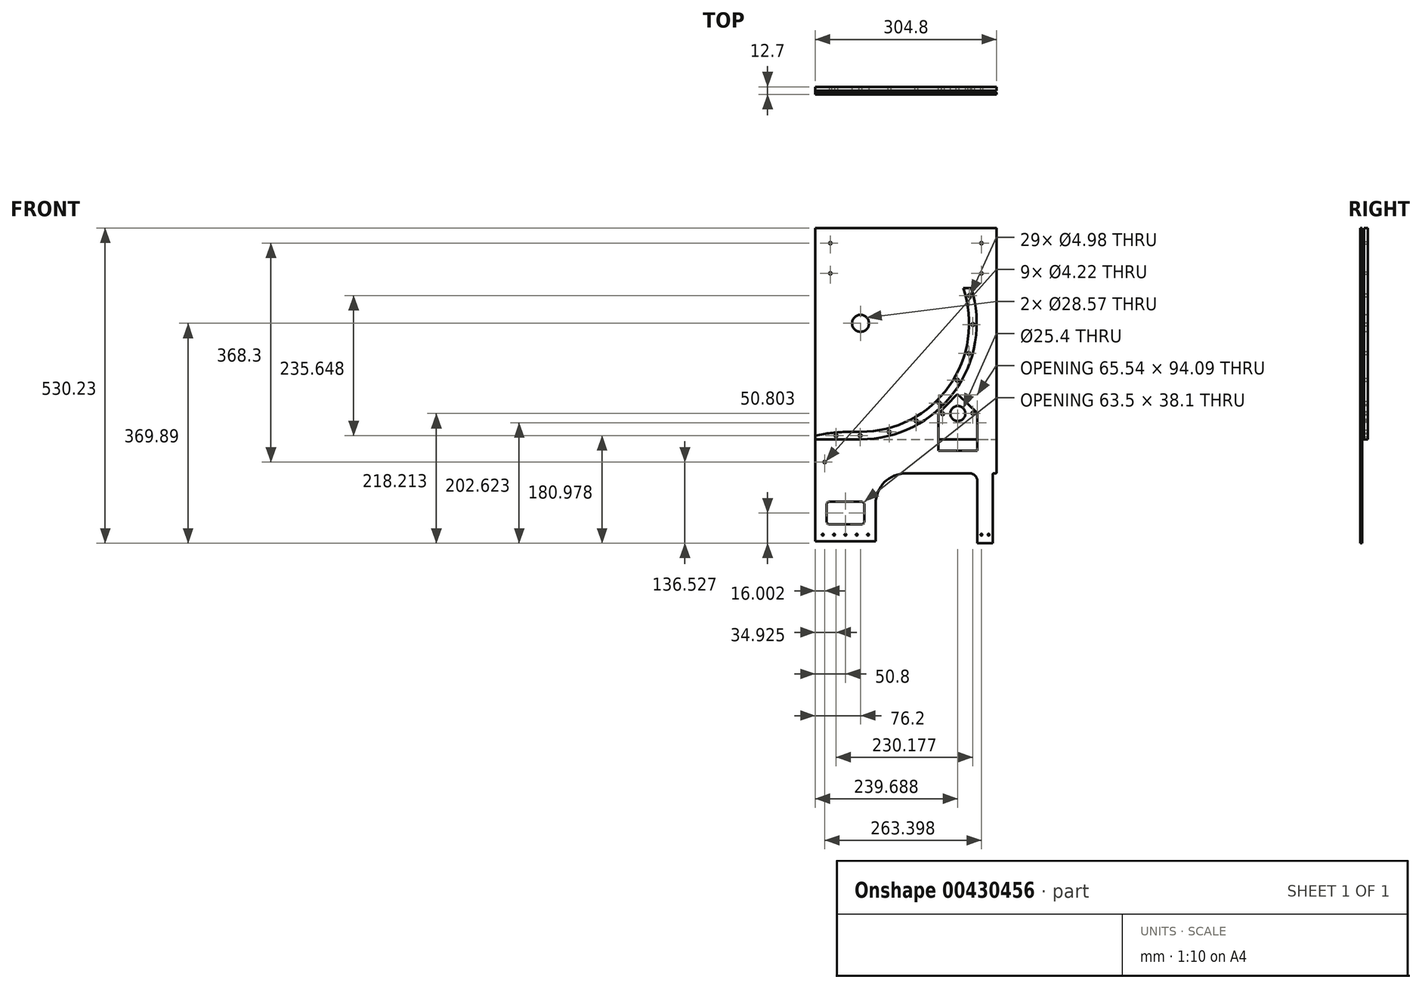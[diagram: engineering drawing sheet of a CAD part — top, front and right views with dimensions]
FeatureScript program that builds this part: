
annotation { "Feature Type Name" : "Feature", "Feature Type Description" : "" }
export const myFeature = defineFeature(function(context is Context, id is Id, definition is map)
    precondition{}
    {
        {
            var Q0;
            Q0=qCreatedBy(makeId("Front.planeOp"),FACE);
            var sketch = newSketch(context, id + "F0", { "sketchPlane" : qUnion([Q0])});
            skCircle(sketch, "E0", {"center": v(0, 0) * mm, "radius": 61.91 * mm, "construction": true});
            skArc(sketch, "E1", {"start": v(0, -182.56) * mm, "mid": v(148.63, -106.01) * mm, "end": v(172.62, 59.44) * mm});
            skLineSegment(sketch, "E2", {"start": v(228.6, -195.26) * mm, "end": v(228.6, 59.44) * mm, "construction": true});
            skLineSegment(sketch, "E3", {"start": v(228.6, 59.44) * mm, "end": v(172.62, 59.44) * mm});
            skLineSegment(sketch, "E4", {"start": v(0, 0) * mm, "end": v(182.56, 0) * mm, "construction": true});
            skLineSegment(sketch, "E5", {"start": v(0, 0) * mm, "end": v(172.62, 59.44) * mm, "construction": true});
            skLineSegment(sketch, "E6", {"start": v(209.55, -195.26) * mm, "end": v(209.55, 59.44) * mm, "construction": true});
            skPoint(sketch, "E7.middle", {"position": v(163.49, -151.68) * mm});
            skLineSegment(sketch, "E8.top", {"start": v(228.6, -195.26) * mm, "end": v(-76.2, -195.26) * mm});
            skLineSegment(sketch, "E8.right", {"start": v(-76.2, -188.91) * mm, "end": v(-76.2, -195.26) * mm});
            skLineSegment(sketch, "E9", {"start": v(0, -182.56) * mm, "end": v(-41.27, -182.56) * mm});
            skCircle(sketch, "E10", {"center": v(163.49, -151.68) * mm, "radius": 25.4 * mm, "construction": true});
            skLineSegment(sketch, "E11", {"start": v(130.72, -152.33) * mm, "end": v(162.84, -118.9) * mm, "construction": true});
            skLineSegment(sketch, "E12", {"start": v(162.84, -118.9) * mm, "end": v(196.26, -151.03) * mm, "construction": true});
            skLineSegment(sketch, "E13", {"start": v(196.26, -151.03) * mm, "end": v(164.14, -184.45) * mm, "construction": true});
            skLineSegment(sketch, "E14", {"start": v(164.14, -184.45) * mm, "end": v(130.72, -152.33) * mm, "construction": true});
            skLineSegment(sketch, "E15", {"start": v(162.84, -118.9) * mm, "end": v(164.14, -184.45) * mm, "construction": true});
            skCircle(sketch, "E16", {"center": v(183.04, 46.74) * mm, "radius": 2.49 * mm});
            skCircle(sketch, "E17.1.0", {"center": v(188.9, -2) * mm, "radius": 2.49 * mm});
            skCircle(sketch, "E17.2.0", {"center": v(182.01, -50.6) * mm, "radius": 2.49 * mm});
            skCircle(sketch, "E17.3.0", {"center": v(162.84, -95.77) * mm, "radius": 2.49 * mm});
            skCircle(sketch, "E17.4.0", {"center": v(132.67, -134.49) * mm, "radius": 2.49 * mm});
            skCircle(sketch, "E17.5.0", {"center": v(93.54, -164.13) * mm, "radius": 2.49 * mm});
            skCircle(sketch, "E17.6.0", {"center": v(48.1, -182.69) * mm, "radius": 2.49 * mm});
            skCircle(sketch, "E17.7.0", {"center": v(-0.58, -188.91) * mm, "radius": 2.49 * mm});
            skLineSegment(sketch, "E17.anchor1", {"start": v(0, 0) * mm, "end": v(183.04, 46.74) * mm, "construction": true});
            skLineSegment(sketch, "E17.anchor2", {"start": v(0, 0) * mm, "end": v(-0.58, -188.91) * mm, "construction": true});
            skLineSegment(sketch, "E18", {"start": v(130.72, -152.33) * mm, "end": v(130.72, -195.26) * mm, "construction": true});
            skLineSegment(sketch, "E19", {"start": v(196.26, -151.03) * mm, "end": v(196.26, -195.26) * mm, "construction": true});
            skCircle(sketch, "E20", {"center": v(-41.27, -188.91) * mm, "radius": 2.49 * mm});
            skLineSegment(sketch, "E21", {"start": v(-76.2, -188.91) * mm, "end": v(-41.27, -182.56) * mm});
            skArc(sketch, "E22.trimOffspring", {"start": v(0, -195.26) * mm, "mid": v(157.7, -115.16) * mm, "end": v(186, 59.44) * mm});
            skPoint(sketch, "E23.orphan", {"position": v(-76.2, -182.56) * mm});
            skSolve(sketch);
        }
        {
            var Q0;
            {var subQ1=sQuery(id+"F0.wireOp",EDGE,"E8.top");var subQ5=sQuery(id+"F0.wireOp",EDGE,"E8.right");var subQ6=makeQuery(id+"F0.imprint","INTERSECT",VERTEX,{"derivedFrom":[subQ1,subQ5]});Q0=makeQuery(id+"F0.imprint","IMPRINT",FACE,{"disambiguationData":[TD([[makeQuery(id+"F0.imprint","IMPRINT",EDGE,{"disambiguationData":[TD([[subQ6,1.0]])],"derivedFrom":subQ1}),-1.0]])]});}
            var Q1;
            {var subQ0=sQuery(id+"F0.wireOp",EDGE,"E1");Q1=makeQuery(id+"F0.imprint","IMPRINT",FACE,{"disambiguationData":[TD([[makeQuery(id+"F0.imprint","IMPRINT",EDGE,{"derivedFrom":subQ0}),-1.0]])]});}
            extrude(context, id + "F1", {"entities" : qUnion([Q0, Q1]), "depth" : 6.35 * mm, "offsetDistance" : 25.4 * mm});
        }
        {
            var Q0;
            {var subQ0=sQuery(id+"F0.wireOp",EDGE,"E1");Q0=makeQuery(id+"F0.imprint","IMPRINT",FACE,{"disambiguationData":[TD([[makeQuery(id+"F0.imprint","IMPRINT",EDGE,{"derivedFrom":subQ0}),-1.0]])]});}
            var sketch = newSketch(context, id + "F2", { "sketchPlane" : qUnion([Q0])});
            skCircle(sketch, "E24", {"center": v(0, 0) * mm, "radius": 14.29 * mm});
            skLineSegment(sketch, "E25.bottom", {"start": v(-76.2, -252.41) * mm, "end": v(228.6, -252.41) * mm});
            skLineSegment(sketch, "E25.top", {"start": v(-76.2, 160.34) * mm, "end": v(228.6, 160.34) * mm});
            skLineSegment(sketch, "E25.left", {"start": v(-76.2, -252.41) * mm, "end": v(-76.2, 160.34) * mm});
            skLineSegment(sketch, "E25.right", {"start": v(228.6, -252.41) * mm, "end": v(228.6, 160.34) * mm});
            skPoint(sketch, "E26.0", {"position": v(183.04, 46.74) * mm});
            skCircle(sketch, "E27.0", {"center": v(188.9, -2) * mm, "radius": 2.49 * mm});
            skCircle(sketch, "E27.1", {"center": v(183.04, 46.74) * mm, "radius": 2.49 * mm});
            skCircle(sketch, "E27.2", {"center": v(182.01, -50.6) * mm, "radius": 2.49 * mm});
            skCircle(sketch, "E27.3", {"center": v(162.84, -95.77) * mm, "radius": 2.49 * mm});
            skCircle(sketch, "E27.4", {"center": v(132.67, -134.49) * mm, "radius": 2.49 * mm});
            skCircle(sketch, "E27.5", {"center": v(93.54, -164.13) * mm, "radius": 2.49 * mm});
            skCircle(sketch, "E27.6", {"center": v(48.1, -182.69) * mm, "radius": 2.49 * mm});
            skCircle(sketch, "E27.7", {"center": v(-0.58, -188.91) * mm, "radius": 2.49 * mm});
            skCircle(sketch, "E27.8", {"center": v(-41.27, -188.91) * mm, "radius": 2.49 * mm});
            skCircle(sketch, "E28.0", {"center": v(163.49, -151.68) * mm, "radius": 25.4 * mm, "construction": true});
            skPoint(sketch, "E29.0", {"position": v(130.72, -152.33) * mm});
            skPoint(sketch, "E29.1", {"position": v(196.26, -151.03) * mm});
            skLineSegment(sketch, "E30", {"start": v(130.72, -152.33) * mm, "end": v(196.26, -151.03) * mm, "construction": true});
            skCircle(sketch, "E31", {"center": v(138.1, -152.18) * mm, "radius": 2.49 * mm});
            skCircle(sketch, "E32", {"center": v(188.88, -151.17) * mm, "radius": 2.49 * mm});
            skCircle(sketch, "E33", {"center": v(346.2, -207.96) * mm, "radius": 2.1 * mm});
            skLineSegment(sketch, "E34.bottom", {"start": v(-76.2, -195.26) * mm, "end": v(381, -195.26) * mm});
            skLineSegment(sketch, "E34.top", {"start": v(-76.2, -252.41) * mm, "end": v(381, -252.41) * mm});
            skLineSegment(sketch, "E34.left", {"start": v(-76.2, -195.26) * mm, "end": v(-76.2, -252.41) * mm});
            skLineSegment(sketch, "E34.right", {"start": v(381, -195.26) * mm, "end": v(381, -252.41) * mm});
            skCircle(sketch, "E35.0.1.0", {"center": v(346.2, -233.36) * mm, "radius": 2.1 * mm});
            skCircle(sketch, "E35.1.0.0", {"center": v(320.8, -207.96) * mm, "radius": 2.1 * mm});
            skCircle(sketch, "E35.1.1.0", {"center": v(320.8, -233.36) * mm, "radius": 2.1 * mm});
            skCircle(sketch, "E35.2.0.0", {"center": v(295.4, -207.96) * mm, "radius": 2.1 * mm});
            skCircle(sketch, "E35.2.1.0", {"center": v(295.4, -233.36) * mm, "radius": 2.1 * mm});
            skCircle(sketch, "E35.3.0.0", {"center": v(270, -207.96) * mm, "radius": 2.1 * mm});
            skCircle(sketch, "E35.3.1.0", {"center": v(270, -233.36) * mm, "radius": 2.1 * mm});
            skCircle(sketch, "E35.4.0.0", {"center": v(244.6, -207.96) * mm, "radius": 2.1 * mm});
            skCircle(sketch, "E35.4.1.0", {"center": v(244.6, -233.36) * mm, "radius": 2.1 * mm});
            skCircle(sketch, "E35.5.0.0", {"center": v(219.2, -207.96) * mm, "radius": 2.1 * mm});
            skCircle(sketch, "E35.5.1.0", {"center": v(219.2, -233.36) * mm, "radius": 2.1 * mm});
            skCircle(sketch, "E35.6.0.0", {"center": v(193.8, -207.96) * mm, "radius": 2.1 * mm});
            skCircle(sketch, "E35.6.1.0", {"center": v(193.8, -233.36) * mm, "radius": 2.1 * mm});
            skCircle(sketch, "E35.7.0.0", {"center": v(168.4, -207.96) * mm, "radius": 2.1 * mm});
            skCircle(sketch, "E35.7.1.0", {"center": v(168.4, -233.36) * mm, "radius": 2.1 * mm});
            skCircle(sketch, "E35.8.0.0", {"center": v(143, -207.96) * mm, "radius": 2.1 * mm});
            skCircle(sketch, "E35.8.1.0", {"center": v(143, -233.36) * mm, "radius": 2.1 * mm});
            skCircle(sketch, "E35.9.0.0", {"center": v(117.6, -207.96) * mm, "radius": 2.1 * mm});
            skCircle(sketch, "E35.9.1.0", {"center": v(117.6, -233.36) * mm, "radius": 2.1 * mm});
            skCircle(sketch, "E35.10.0.0", {"center": v(92.2, -207.96) * mm, "radius": 2.1 * mm});
            skCircle(sketch, "E35.10.1.0", {"center": v(92.2, -233.36) * mm, "radius": 2.1 * mm});
            skCircle(sketch, "E35.11.0.0", {"center": v(66.8, -207.96) * mm, "radius": 2.1 * mm});
            skCircle(sketch, "E35.11.1.0", {"center": v(66.8, -233.36) * mm, "radius": 2.1 * mm});
            skCircle(sketch, "E35.12.0.0", {"center": v(41.4, -207.96) * mm, "radius": 2.1 * mm});
            skCircle(sketch, "E35.12.1.0", {"center": v(41.4, -233.36) * mm, "radius": 2.1 * mm});
            skCircle(sketch, "E35.13.0.0", {"center": v(16, -207.96) * mm, "radius": 2.1 * mm});
            skCircle(sketch, "E35.13.1.0", {"center": v(16, -233.36) * mm, "radius": 2.1 * mm});
            skCircle(sketch, "E35.14.0.0", {"center": v(-9.4, -207.96) * mm, "radius": 2.1 * mm});
            skCircle(sketch, "E35.14.1.0", {"center": v(-9.4, -233.36) * mm, "radius": 2.1 * mm});
            skCircle(sketch, "E35.15.0.0", {"center": v(-34.8, -207.96) * mm, "radius": 2.1 * mm});
            skCircle(sketch, "E35.15.1.0", {"center": v(-34.8, -233.36) * mm, "radius": 2.1 * mm});
            skCircle(sketch, "E35.16.0.0", {"center": v(-60.2, -207.96) * mm, "radius": 2.1 * mm});
            skCircle(sketch, "E35.16.1.0", {"center": v(-60.2, -233.36) * mm, "radius": 2.1 * mm});
            skLineSegment(sketch, "E35.direction1", {"start": v(346.2, -207.96) * mm, "end": v(320.8, -207.96) * mm, "construction": true});
            skLineSegment(sketch, "E35.direction2", {"start": v(346.2, -207.96) * mm, "end": v(346.2, -233.36) * mm, "construction": true});
            skCircle(sketch, "E36", {"center": v(163.49, -151.68) * mm, "radius": 12.7 * mm});
            skLineSegment(sketch, "E37", {"start": v(-50.8, 160.34) * mm, "end": v(-50.8, -195.26) * mm, "construction": true});
            skCircle(sketch, "E38", {"center": v(-50.8, 84.14) * mm, "radius": 2.1 * mm});
            skCircle(sketch, "E39.0.1.0", {"center": v(-50.8, 134.94) * mm, "radius": 2.1 * mm});
            skLineSegment(sketch, "E39.direction1", {"start": v(-50.8, 84.14) * mm, "end": v(-50.8, 84.14) * mm});
            skLineSegment(sketch, "E39.direction2", {"start": v(-50.8, 84.14) * mm, "end": v(-50.8, 134.94) * mm, "construction": true});
            skLineSegment(sketch, "E40", {"start": v(76.2, 160.34) * mm, "end": v(76.2, -195.26) * mm, "construction": true});
            skCircle(sketch, "E41.MirrorC", {"center": v(203.2, 84.14) * mm, "radius": 2.1 * mm});
            skCircle(sketch, "E42.MirrorC", {"center": v(203.2, 134.94) * mm, "radius": 2.1 * mm});
            skLineSegment(sketch, "E43.MirrorCS", {"start": v(203.2, 84.14) * mm, "end": v(203.2, 134.94) * mm, "construction": true});
            skLineSegment(sketch, "E44.0", {"start": v(0, -182.56) * mm, "end": v(-41.27, -182.56) * mm});
            skSolve(sketch);
        }
        {
            var Q0;
            {var subQ3=sQuery(id+"F2.wireOp",EDGE,"E34.left");Q0=makeQuery(id+"F2.imprint","IMPRINT",FACE,{"disambiguationData":[TD([[makeQuery(id+"F2.imprint","IMPRINT",EDGE,{"derivedFrom":subQ3}),1.0]])]});}
            var Q1;
            Q1=makeQuery(id+"F2.imprint","IMPRINT",FACE,{"disambiguationData":[TD([[makeQuery(id+"F2.imprint","IMPRINT",EDGE,{"derivedFrom":sQuery(id+"F2.wireOp",EDGE,"E24")}),-1.0]])]});
            var Q2;
            Q2=makeQuery(id+"F2.imprint","IMPRINT",FACE,{"disambiguationData":[TD([[makeQuery(id+"F2.imprint","IMPRINT",EDGE,{"derivedFrom":sQuery(id+"F2.wireOp",EDGE,"E27.0")}),-1.0]])]});
            var Q3;
            {var subQ1=sQuery(id+"F0.wireOp",EDGE,"E21");var subQ2=makeQuery(id+"F0.imprint","INTERSECT",VERTEX,{"derivedFrom":[sQuery(id+"F0.wireOp",EDGE,"qDOghrOL-mCar-WwbD-ljMS-Sb26vS9t9zeY"),subQ1]});var subQ3=makeQuery(id+"F0.imprint","IMPRINT",EDGE,{"disambiguationData":[TD([[subQ2,1.0]])],"derivedFrom":subQ1});Q3=makeQuery(id+"F2.imprint","IMPRINT",FACE,{"disambiguationData":[TD([[makeQuery(id+"F2.imprint","IMPRINT",EDGE,{"derivedFrom":subQ3}),1.0]])]});}
            extrude(context, id + "F3", {"entities" : qUnion([Q0, Q1, Q2, Q3]), "oppositeDirection" : true, "depth" : 6.35 * mm, "offsetDistance" : 25.4 * mm});
        }
        {
            var Q0;
            Q0=makeQuery(id+"F1.opExtrude","CAP_FACE",FACE,{"disambiguationData":[OSD([sQuery(id+"F0.wireOp",EDGE,"E1"),sQuery(id+"F0.wireOp",EDGE,"E3"),sQuery(id+"F0.wireOp",EDGE,"E8.top"),sQuery(id+"F0.wireOp",EDGE,"E8.right"),sQuery(id+"F0.wireOp",EDGE,"E9"),sQuery(id+"F0.wireOp",EDGE,"E16"),sQuery(id+"F0.wireOp",EDGE,"E17.1.0"),sQuery(id+"F0.wireOp",EDGE,"E17.2.0"),sQuery(id+"F0.wireOp",EDGE,"E17.3.0"),sQuery(id+"F0.wireOp",EDGE,"E17.4.0"),sQuery(id+"F0.wireOp",EDGE,"E17.5.0"),sQuery(id+"F0.wireOp",EDGE,"E17.6.0"),sQuery(id+"F0.wireOp",EDGE,"E17.7.0"),sQuery(id+"F0.wireOp",EDGE,"qDOghrOL-mCar-WwbD-ljMS-Sb26vS9t9zeY"),sQuery(id+"F0.wireOp",EDGE,"E20")])],"isStart":false});
            var sketch = newSketch(context, id + "F4", { "sketchPlane" : qUnion([Q0])});
            skCircle(sketch, "E45.0", {"center": v(0, 0) * mm, "radius": 14.29 * mm});
            skCircle(sketch, "E46.0", {"center": v(162.84, -95.77) * mm, "radius": 2.49 * mm});
            skCircle(sketch, "E47.0", {"center": v(182.01, -50.6) * mm, "radius": 2.49 * mm});
            skCircle(sketch, "E47.1", {"center": v(188.9, -2) * mm, "radius": 2.49 * mm});
            skCircle(sketch, "E47.2", {"center": v(183.04, 46.74) * mm, "radius": 2.49 * mm});
            skCircle(sketch, "E47.3", {"center": v(132.67, -134.49) * mm, "radius": 2.49 * mm});
            skCircle(sketch, "E47.4", {"center": v(93.54, -164.13) * mm, "radius": 2.49 * mm});
            skCircle(sketch, "E47.5", {"center": v(48.1, -182.69) * mm, "radius": 2.49 * mm});
            skCircle(sketch, "E47.6", {"center": v(-0.58, -188.91) * mm, "radius": 2.49 * mm});
            skCircle(sketch, "E47.7", {"center": v(-41.27, -188.91) * mm, "radius": 2.49 * mm});
            skPoint(sketch, "E48.0", {"position": v(-76.2, 160.34) * mm});
            skLineSegment(sketch, "E49", {"start": v(-76.2, 160.34) * mm, "end": v(-76.2, -369.89) * mm});
            skPoint(sketch, "E50.0", {"position": v(228.6, -252.41) * mm});
            skLineSegment(sketch, "E51.bottom", {"start": v(-76.2, -369.89) * mm, "end": v(222.25, -369.89) * mm});
            skLineSegment(sketch, "E51.top", {"start": v(76.2, -252.41) * mm, "end": v(228.6, -252.41) * mm});
            skLineSegment(sketch, "E51.left", {"start": v(-76.2, -369.89) * mm, "end": v(-76.2, -252.41) * mm});
            skCircle(sketch, "E52.0", {"center": v(-60.2, -233.36) * mm, "radius": 2.1 * mm});
            skLineSegment(sketch, "E53", {"start": v(25.4, -369.89) * mm, "end": v(25.4, -303.21) * mm});
            skArc(sketch, "E54.filletArc", {"start": v(76.2, -252.41) * mm, "mid": v(40.28, -267.3) * mm, "end": v(25.4, -303.21) * mm});
            skPoint(sketch, "E55.0", {"position": v(76.2, 160.34) * mm});
            skLineSegment(sketch, "E56.0", {"start": v(-76.2, 160.34) * mm, "end": v(222.25, 160.34) * mm});
            skLineSegment(sketch, "E57.0", {"start": v(165.13, -121.1) * mm, "end": v(195.28, -150.09) * mm});
            skLineSegment(sketch, "E58.0", {"start": v(131.6, -151.4) * mm, "end": v(160.64, -121.2) * mm});
            skLineSegment(sketch, "E59.0", {"start": v(164.14, -184.45) * mm, "end": v(130.72, -152.33) * mm});
            skLineSegment(sketch, "E60.0", {"start": v(196.26, -151.03) * mm, "end": v(164.14, -184.45) * mm});
            skLineSegment(sketch, "E61.bottom", {"start": v(-76.2, -369.89) * mm, "end": v(25.4, -369.89) * mm});
            skLineSegment(sketch, "E61.top", {"start": v(-76.2, -344.49) * mm, "end": v(25.4, -344.49) * mm});
            skLineSegment(sketch, "E61.left", {"start": v(-76.2, -369.89) * mm, "end": v(-76.2, -344.49) * mm});
            skLineSegment(sketch, "E61.right", {"start": v(25.4, -369.89) * mm, "end": v(25.4, -344.49) * mm});
            skLineSegment(sketch, "E62", {"start": v(-76.2, -366.71) * mm, "end": v(25.4, -366.71) * mm});
            skLineSegment(sketch, "E63", {"start": v(-25.4, -366.71) * mm, "end": v(-25.4, -344.49) * mm, "construction": true});
            skCircle(sketch, "E64", {"center": v(-25.4, -355.6) * mm, "radius": 1.59 * mm});
            skLineSegment(sketch, "E65.direction1", {"start": v(-25.4, -355.6) * mm, "end": v(-6.35, -355.6) * mm, "construction": true});
            skCircle(sketch, "E66.MirrorC", {"center": v(-63.5, -355.6) * mm, "radius": 1.59 * mm});
            skCircle(sketch, "E67.MirrorC", {"center": v(-44.45, -355.6) * mm, "radius": 1.59 * mm});
            skLineSegment(sketch, "E68", {"start": v(130.72, -153.6) * mm, "end": v(130.72, -252.41) * mm});
            skLineSegment(sketch, "E69", {"start": v(196.26, -152.38) * mm, "end": v(196.26, -252.41) * mm});
            skPoint(sketch, "E70.visualSharp", {"position": v(162.84, -118.9) * mm});
            skArc(sketch, "E70.filletArc", {"start": v(165.13, -121.1) * mm, "mid": v(162.86, -120.22) * mm, "end": v(160.64, -121.2) * mm});
            skPoint(sketch, "E71.visualSharp", {"position": v(130.72, -152.33) * mm});
            skArc(sketch, "E71.filletArc", {"start": v(131.6, -151.4) * mm, "mid": v(130.95, -152.42) * mm, "end": v(130.72, -153.6) * mm});
            skPoint(sketch, "E72.visualSharp", {"position": v(196.26, -151.03) * mm});
            skArc(sketch, "E72.filletArc", {"start": v(196.26, -152.38) * mm, "mid": v(196, -151.13) * mm, "end": v(195.28, -150.09) * mm});
            skCircle(sketch, "E73.1", {"center": v(-50.8, 134.94) * mm, "radius": 2.1 * mm});
            skCircle(sketch, "E73.2", {"center": v(-50.8, 84.14) * mm, "radius": 2.1 * mm});
            skCircle(sketch, "E73.3", {"center": v(203.2, 84.14) * mm, "radius": 2.1 * mm});
            skCircle(sketch, "E73.5", {"center": v(203.2, 134.94) * mm, "radius": 2.1 * mm});
            skLineSegment(sketch, "E74", {"start": v(196.26, -252.41) * mm, "end": v(196.26, -369.89) * mm});
            skLineSegment(sketch, "E75", {"start": v(196.26, -366.71) * mm, "end": v(222.25, -366.71) * mm});
            skLineSegment(sketch, "E76", {"start": v(196.26, -344.49) * mm, "end": v(222.25, -344.49) * mm});
            skCircle(sketch, "E77.0.1.0", {"center": v(-6.35, -355.6) * mm, "radius": 1.59 * mm});
            skCircle(sketch, "E78.0.2.0", {"center": v(12.7, -355.6) * mm, "radius": 1.59 * mm});
            skCircle(sketch, "E79.0.12.0", {"center": v(203.2, -355.6) * mm, "radius": 1.59 * mm});
            skLineSegment(sketch, "E80", {"start": v(130.72, -214.31) * mm, "end": v(196.26, -214.31) * mm});
            skLineSegment(sketch, "E81.bottom", {"start": v(-57.15, -338.14) * mm, "end": v(6.35, -338.14) * mm});
            skLineSegment(sketch, "E81.top", {"start": v(-57.15, -300.04) * mm, "end": v(6.35, -300.04) * mm});
            skLineSegment(sketch, "E81.left", {"start": v(-57.15, -338.14) * mm, "end": v(-57.15, -300.04) * mm});
            skLineSegment(sketch, "E81.right", {"start": v(6.35, -338.14) * mm, "end": v(6.35, -300.04) * mm});
            skLineSegment(sketch, "E82", {"start": v(222.25, 160.34) * mm, "end": v(222.25, -369.89) * mm});
            skPoint(sketch, "E83.orphan", {"position": v(228.6, 160.34) * mm});
            skCircle(sketch, "E84", {"center": v(215.3, -355.6) * mm, "radius": 1.59 * mm});
            skLineSegment(sketch, "E85", {"start": v(203.2, -355.6) * mm, "end": v(196.26, -355.6) * mm, "construction": true});
            skLineSegment(sketch, "E86", {"start": v(215.3, -355.6) * mm, "end": v(222.25, -355.6) * mm, "construction": true});
            skLineSegment(sketch, "E87.bottom", {"start": v(222.25, 160.34) * mm, "end": v(228.6, 160.34) * mm});
            skLineSegment(sketch, "E87.top", {"start": v(222.25, -252.41) * mm, "end": v(228.6, -252.41) * mm});
            skLineSegment(sketch, "E87.left", {"start": v(222.25, 160.34) * mm, "end": v(222.25, -252.41) * mm});
            skLineSegment(sketch, "E87.right", {"start": v(228.6, 160.34) * mm, "end": v(228.6, -252.41) * mm});
            skSolve(sketch);
        }
        {
            var Q0;
            Q0=makeQuery(id+"F4.imprint","IMPRINT",FACE,{"disambiguationData":[TD([[makeQuery(id+"F4.imprint","IMPRINT",EDGE,{"derivedFrom":sQuery(id+"F4.wireOp",EDGE,"E46.0")}),-1.0]])]});
            var Q1;
            Q1=makeQuery(id+"F4.imprint","IMPRINT",FACE,{"disambiguationData":[TD([[makeQuery(id+"F4.imprint","IMPRINT",EDGE,{"derivedFrom":sQuery(id+"F4.wireOp",EDGE,"E45.0")}),-1.0]])]});
            var Q2;
            {var subQ5=sQuery(id+"F4.wireOp",EDGE,"E80");Q2=makeQuery(id+"F4.imprint","IMPRINT",FACE,{"disambiguationData":[TD([[makeQuery(id+"F4.imprint","IMPRINT",EDGE,{"derivedFrom":subQ5}),-1.0]])]});}
            var Q3;
            {var subQ5=sQuery(id+"F4.wireOp",EDGE,"E76");Q3=makeQuery(id+"F4.imprint","IMPRINT",FACE,{"disambiguationData":[TD([[makeQuery(id+"F4.imprint","IMPRINT",EDGE,{"derivedFrom":subQ5}),1.0]])]});}
            var Q4;
            {var subQ1=sQuery(id+"F4.wireOp",EDGE,"E61.top");Q4=makeQuery(id+"F4.imprint","IMPRINT",FACE,{"disambiguationData":[TD([[makeQuery(id+"F4.imprint","IMPRINT",EDGE,{"derivedFrom":subQ1}),-1.0]])]});}
            var Q5;
            {var subQ1=sQuery(id+"F4.wireOp",EDGE,"E75");Q5=makeQuery(id+"F4.imprint","IMPRINT",FACE,{"disambiguationData":[TD([[makeQuery(id+"F4.imprint","IMPRINT",EDGE,{"derivedFrom":subQ1}),1.0]])]});}
            var Q6;
            {var subQ5=sQuery(id+"F4.wireOp",EDGE,"E75");Q6=makeQuery(id+"F4.imprint","IMPRINT",FACE,{"disambiguationData":[TD([[makeQuery(id+"F4.imprint","IMPRINT",EDGE,{"derivedFrom":subQ5}),-1.0]])]});}
            var Q7;
            {var subQ0=sQuery(id+"F4.wireOp",EDGE,"E61.bottom");Q7=makeQuery(id+"F4.imprint","IMPRINT",FACE,{"disambiguationData":[TD([[makeQuery(id+"F4.imprint","IMPRINT",EDGE,{"derivedFrom":subQ0}),1.0]])]});}
            var Q8;
            Q8=makeQuery(id+"F4.imprint","IMPRINT",FACE,{"disambiguationData":[TD([[makeQuery(id+"F4.imprint","IMPRINT",EDGE,{"derivedFrom":sQuery(id+"F4.wireOp",EDGE,"E87.bottom")}),-1.0]])]});
            extrude(context, id + "F5", {"entities" : qUnion([Q0, Q1, Q2, Q3, Q4, Q5, Q6, Q7, Q8]), "oppositeDirection" : true, "depth" : 3.17 * mm, "offsetDistance" : 25.4 * mm});
        }
        {
            var Q0;
            Q0=makeQuery(id+"F1.opExtrude","SWEPT_EDGE",EDGE,{"disambiguationData":[OSD([sQuery(id+"F0.wireOp",EDGE,"E9"),sQuery(id+"F0.wireOp",EDGE,"E21")])]});
            fillet(context, id + "F6", {"entities" : qUnion([Q0]), "radius" : 269.2 * mm, "tangentPropagation" : true, "allowEdgeOverflow" : false});
        }
        {
            var Q0;
            Q0=makeQuery(id+"F5.opExtrude","SWEPT_EDGE",EDGE,{"disambiguationData":[OSD([sQuery(id+"F4.wireOp",EDGE,"E51.top"),sQuery(id+"F4.wireOp",EDGE,"E69"),sQuery(id+"F4.wireOp",EDGE,"E74")])]});
            fillet(context, id + "F7", {"entities" : qUnion([Q0]), "radius" : 12.7 * mm, "tangentPropagation" : true, "allowEdgeOverflow" : false});
        }
        {
            var Q0;
            Q0=makeQuery(id+"F5.opExtrude","SWEPT_EDGE",EDGE,{"disambiguationData":[OSD([sQuery(id+"F4.wireOp",EDGE,"E81.top"),sQuery(id+"F4.wireOp",EDGE,"E81.right")])]});
            var Q1;
            Q1=makeQuery(id+"F5.opExtrude","SWEPT_EDGE",EDGE,{"disambiguationData":[OSD([sQuery(id+"F4.wireOp",EDGE,"E81.top"),sQuery(id+"F4.wireOp",EDGE,"E81.left")])]});
            var Q2;
            Q2=makeQuery(id+"F5.opExtrude","SWEPT_EDGE",EDGE,{"disambiguationData":[OSD([sQuery(id+"F4.wireOp",EDGE,"E81.bottom"),sQuery(id+"F4.wireOp",EDGE,"E81.left")])]});
            var Q3;
            Q3=makeQuery(id+"F5.opExtrude","SWEPT_EDGE",EDGE,{"disambiguationData":[OSD([sQuery(id+"F4.wireOp",EDGE,"E81.bottom"),sQuery(id+"F4.wireOp",EDGE,"E81.right")])]});
            fillet(context, id + "F8", {"entities" : qUnion([Q0, Q1, Q2, Q3]), "radius" : 5.08 * mm, "tangentPropagation" : true, "allowEdgeOverflow" : false});
        }
        {
            var Q0;
            Q0=makeQuery(id+"F5.opExtrude","SWEPT_EDGE",EDGE,{"disambiguationData":[OSD([sQuery(id+"F4.wireOp",EDGE,"E87.top"),sQuery(id+"F4.wireOp",EDGE,"E87.right")])]});
            var Q1;
            Q1=makeQuery(id+"F5.opExtrude","SWEPT_EDGE",EDGE,{"disambiguationData":[OSD([sQuery(id+"F4.wireOp",EDGE,"E51.top"),sQuery(id+"F4.wireOp",EDGE,"E82"),sQuery(id+"F4.wireOp",EDGE,"E87.top"),sQuery(id+"F4.wireOp",EDGE,"E87.left")])]});
            fillet(context, id + "F9", {"entities" : qUnion([Q0, Q1]), "radius" : 1.27 * mm, "tangentPropagation" : true, "allowEdgeOverflow" : false});
        }
    });
